# Revit family: VLGFP2001-5NDWSxxxxxxxx-RF
name_source: partatom
category: Leuchten
units: mm (PartAtom-declared; Revit-internal decimal feet)

## family parameters
Basisbauteil = Fläche
Beim Laden mit Abzugskörper schneiden = Nein
Bemaßung runder Anschluss = Durchmesser verwenden
Gemeinsam genutzt = Nein
Lichtquelle = Ja
OmniClass-Nummer = 23.80.70.11
OmniClass-Titel = Luminaries for Internal Lighting
Raumberechnungspunkt = Nein
Teiletyp = Normal

## types (6) — shared parameters
Baugruppenkennzeichen = D5020200
Emissionsform beim Rendern sichtbar = Nein
Farbfilter = 16777215
Farbtemperaturverschiebung bei Dämpfen der Lampe = <Keine Auswahl>
Hersteller = RIDI Leuchten GmbH
Lampe = LED
Neigungswinkel = 90.00°
Scheinlast = 74 VA
URL = www.ridi.de
Von Breite des Rechtecks ausssenden = 1969 mm
Von Länge des Rechtecks aussenden = 27 mm  [stored 0.0885827 ft]
brand = RIDI
conformity mark = CE
electrical safety class = 1
height = 66 mm  [stored 0.216535 ft]
ingress protection (IP) code = IP54
length = 2000 mm  [stored 6.56168 ft]
nominal frequency = 50-60Hz
nominal voltage = 230
rated input power = 74
voltage type (AC, DC, UC) = AC
weight = 2,421 kg
width = 67 mm
zero-valued in all types: Vorgabe-Ansicht

## per-type parameters (varying)
| type | Datei für fotometrisches Netz | Modell |
| VLGFP2001-5NDWS830B1100-RF | VLGFP1501-5NDWS840B0800.IES | 1551384 |
| VLGFP2001-5NDWS830E1000-RF | VLGFP1501-5NDWS840E0750.IES | 1551385 |
| VLGFP2001-5NDWS840B1100-RF | VLGFP1501-5NDWS840B0800.IES | 1551386 |
| VLGFP2001-5NDWS840E1100-RF | VLGFP1501-5NDWS840E0750.IES | 1551387 |
| VLGFP2001-5NDWS865B1100-RF | VLGFP1501-5NDWS840B0800.IES | 1551388 |
| VLGFP2001-5NDWS865E1100-RF | VLGFP1501-5NDWS840E0750.IES | 1551389 |

note: column(s) folded — value = type name in every type: product name

note: [stored X ft] marks values corroborated as IEEE doubles in the binary element streams (Revit-internal decimal feet)
